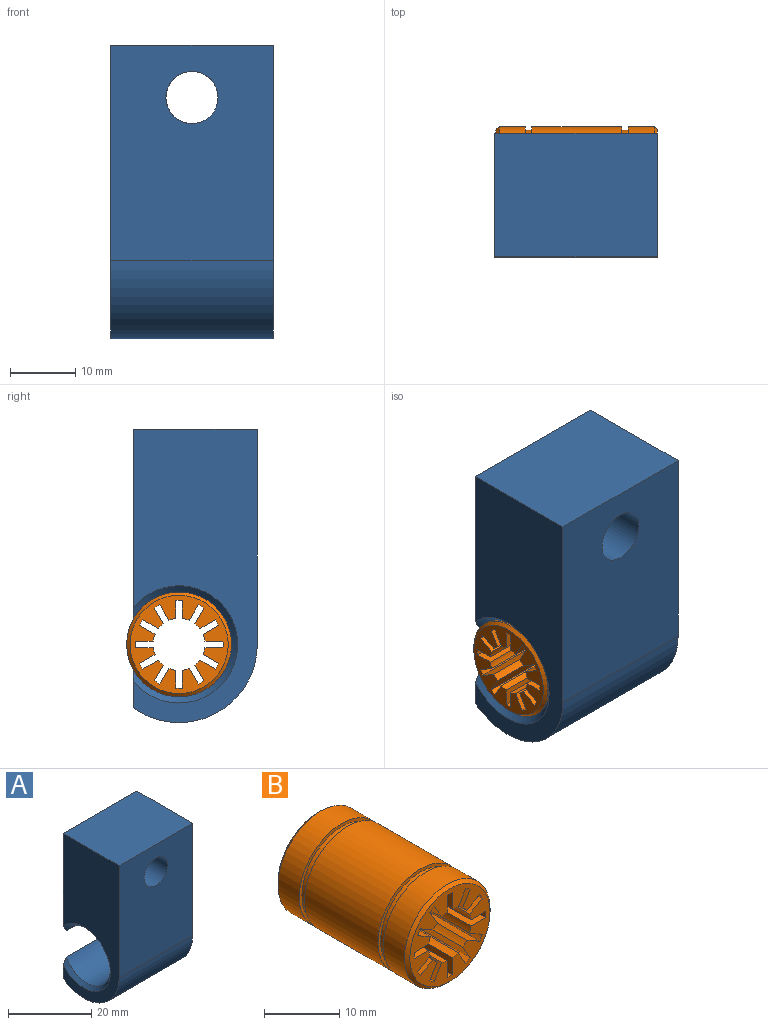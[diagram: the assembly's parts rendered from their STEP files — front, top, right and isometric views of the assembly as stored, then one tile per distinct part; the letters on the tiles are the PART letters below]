
ASSEMBLY  parts=2 mates=1
PART A: 11 faces, bbox 25x19.9x45 mm
  f0: plane 25x19mm, normal (0,0,1), area 475mm2, adj f3,f4,f7,f8
  f1: cylinder r=12mm len=25mm, axis (-1,0,0), area 658.1mm2, adj f3,f4,f7,f9
  f2: cylinder r=8mm len=23mm, axis (-1,0,0), area 970.1mm2, adj f5,f6,f8,f9
  f3: plane 45x19mm, normal (1,0,0), area 580mm2, adj f0,f1,f6,f7,f8,f9
  f4: plane 45x19mm, normal (-1,0,0), area 580mm2, adj f0,f1,f5,f7,f8,f9
  f5: cone r=9mm half-angle=45deg, axis (-1,0,0), area 61.1mm2, adj f2,f4,f8,f9
  f6: cone r=8mm half-angle=45deg, axis (1,0,0), area 61.1mm2, adj f2,f3,f8,f9
  f7: plane 33x25mm, normal (0,-1,0), area 774.7mm2, adj f0,f1,f3,f4,f10
  f8: plane 29.13x25mm, normal (0,1,0), area 676mm2, adj f0,f2,f3,f4,f5,f6,f10
  f9: plane 25x5.87mm, normal (0,1,0), area 145mm2, adj f1,f2,f3,f4,f5,f6
  f10: cylinder r=4mm len=19mm, axis (0,-1,0), area 477.5mm2, adj f7,f8
PART B: 61 faces, bbox 16.1x24.8x16.1 mm
  f0: plane 15.08x15.08mm, normal (0,1,0), area 95.2mm2, adj f12,f13,f14,f15,f16,f17,f18,f19
  f1: cylinder r=8.04mm len=16.08mm, axis (0,1,0), area 202mm2, adj f2,f12
  f2: plane 16.08x16.08mm, normal (0,-1,0), area 24.5mm2, adj f1,f3
  f3: cylinder r=7.54mm len=15.08mm, axis (0,1,0), area 47.4mm2, adj f2,f4
  f4: plane 16.08x16.08mm, normal (0,1,0), area 24.5mm2, adj f3,f5
  f5: cylinder r=8.04mm len=16.08mm, axis (0,1,0), area 697mm2, adj f4,f6
  f6: plane 16.08x16.08mm, normal (0,-1,0), area 24.5mm2, adj f5,f7
  f7: cylinder r=7.54mm len=15.08mm, axis (0,1,0), area 47.4mm2, adj f6,f8
  f8: plane 16.08x16.08mm, normal (0,1,0), area 24.5mm2, adj f7,f9
  f9: cylinder r=8.04mm len=16.08mm, axis (0,1,0), area 202mm2, adj f8,f11
  f10: plane 15.08x15.08mm, normal (0,-1,0), area 95.2mm2, adj f11,f13,f14,f15,f16,f17,f18,f19
  f11: cone r=8.04mm half-angle=45deg, axis (0,1,0), area 34.6mm2, adj f9,f10
  f12: cone r=7.54mm half-angle=45deg, axis (0,-1,0), area 34.6mm2, adj f0,f1
  f13: cylinder r=6.75mm len=24.8mm, axis (0,1,0), area 24.8mm2, adj f0,f10,f14,f60
  f14: plane 24.8x2.76mm, normal (-1,0,0), area 68.5mm2, adj f0,f10,f13,f15
  f15: cylinder r=4mm len=24.8mm, axis (0,1,0), area 27.1mm2, adj f0,f10,f14,f16
  f16: plane 24.8x2.39mm, normal (0.87,0,0.5), area 68.5mm2, adj f0,f10,f15,f17
  f17: cylinder r=6.75mm len=24.8mm, axis (0,1,0), area 24.8mm2, adj f0,f10,f16,f18
  f18: plane 24.8x2.39mm, normal (-0.87,0,-0.5), area 68.5mm2, adj f0,f10,f17,f19
  f19: cylinder r=4mm len=24.8mm, axis (0,1,0), area 27.1mm2, adj f0,f10,f18,f20
  f20: plane 24.8x2.39mm, normal (0.5,0,0.87), area 68.5mm2, adj f0,f10,f19,f21
  f21: cylinder r=6.75mm len=24.8mm, axis (0,1,0), area 24.8mm2, adj f0,f10,f20,f22
  f22: plane 24.8x2.39mm, normal (-0.5,0,-0.87), area 68.5mm2, adj f0,f10,f21,f23
  f23: cylinder r=4mm len=24.8mm, axis (0,1,0), area 27.1mm2, adj f0,f10,f22,f24
  f24: plane 24.8x2.76mm, normal (0,0,1), area 68.5mm2, adj f0,f10,f23,f25
  f25: cylinder r=6.75mm len=24.8mm, axis (0,1,0), area 24.8mm2, adj f0,f10,f24,f26
  f26: plane 24.8x2.76mm, normal (0,0,-1), area 68.5mm2, adj f0,f10,f25,f27
  f27: cylinder r=4mm len=24.8mm, axis (0,1,0), area 27.1mm2, adj f0,f10,f26,f28
  f28: plane 24.8x2.39mm, normal (-0.5,0,0.87), area 68.5mm2, adj f0,f10,f27,f29
  f29: cylinder r=6.75mm len=24.8mm, axis (0,1,0), area 24.8mm2, adj f0,f10,f28,f30
  f30: plane 24.8x2.39mm, normal (0.5,0,-0.87), area 68.5mm2, adj f0,f10,f29,f31
  f31: cylinder r=4mm len=24.8mm, axis (0,1,0), area 27.1mm2, adj f0,f10,f30,f32
  f32: plane 24.8x2.39mm, normal (-0.87,0,0.5), area 68.5mm2, adj f0,f10,f31,f33
  f33: cylinder r=6.75mm len=24.8mm, axis (0,1,0), area 24.8mm2, adj f0,f10,f32,f34
  f34: plane 24.8x2.39mm, normal (0.87,0,-0.5), area 68.5mm2, adj f0,f10,f33,f35
  f35: cylinder r=4mm len=24.8mm, axis (0,1,0), area 27.1mm2, adj f0,f10,f34,f36
  f36: plane 24.8x2.76mm, normal (-1,0,0), area 68.5mm2, adj f0,f10,f35,f37
  f37: cylinder r=6.75mm len=24.8mm, axis (0,1,0), area 24.8mm2, adj f0,f10,f36,f38
  f38: plane 24.8x2.76mm, normal (1,0,0), area 68.5mm2, adj f0,f10,f37,f39
  f39: cylinder r=4mm len=24.8mm, axis (0,1,0), area 27.1mm2, adj f0,f10,f38,f40
  f40: plane 24.8x2.39mm, normal (-0.87,0,-0.5), area 68.5mm2, adj f0,f10,f39,f41
  f41: cylinder r=6.75mm len=24.8mm, axis (0,1,0), area 24.8mm2, adj f0,f10,f40,f42
  f42: plane 24.8x2.39mm, normal (0.87,0,0.5), area 68.5mm2, adj f0,f10,f41,f43
  f43: cylinder r=4mm len=24.8mm, axis (0,1,0), area 27.1mm2, adj f0,f10,f42,f44
  f44: plane 24.8x2.39mm, normal (-0.5,0,-0.87), area 68.5mm2, adj f0,f10,f43,f45
  f45: cylinder r=6.75mm len=24.8mm, axis (0,1,0), area 24.8mm2, adj f0,f10,f44,f46
  f46: plane 24.8x2.39mm, normal (0.5,0,0.87), area 68.5mm2, adj f0,f10,f45,f47
  f47: cylinder r=4mm len=24.8mm, axis (0,1,0), area 27.1mm2, adj f0,f10,f46,f48
  f48: plane 24.8x2.76mm, normal (0,0,-1), area 68.5mm2, adj f0,f10,f47,f49
  f49: cylinder r=6.75mm len=24.8mm, axis (0,1,0), area 24.8mm2, adj f0,f10,f48,f50
  f50: plane 24.8x2.76mm, normal (0,0,1), area 68.5mm2, adj f0,f10,f49,f51
  f51: cylinder r=4mm len=24.8mm, axis (0,1,0), area 27.1mm2, adj f0,f10,f50,f52
  f52: plane 24.8x2.39mm, normal (0.5,0,-0.87), area 68.5mm2, adj f0,f10,f51,f53
  f53: cylinder r=6.75mm len=24.8mm, axis (0,1,0), area 24.8mm2, adj f0,f10,f52,f54
  f54: plane 24.8x2.39mm, normal (-0.5,0,0.87), area 68.5mm2, adj f0,f10,f53,f55
  f55: cylinder r=4mm len=24.8mm, axis (0,1,0), area 27.1mm2, adj f0,f10,f54,f56
  f56: plane 24.8x2.39mm, normal (0.87,0,-0.5), area 68.5mm2, adj f0,f10,f55,f57
  f57: cylinder r=6.75mm len=24.8mm, axis (0,1,0), area 24.8mm2, adj f0,f10,f56,f58
  f58: plane 24.8x2.39mm, normal (-0.87,0,0.5), area 68.5mm2, adj f0,f10,f57,f59
  f59: cylinder r=4mm len=24.8mm, axis (0,1,0), area 27.1mm2, adj f0,f10,f58,f60
  f60: plane 24.8x2.76mm, normal (1,0,0), area 68.5mm2, adj f0,f10,f13,f59
PLACE A t=(0.24,8.7,-10.65)mm
PLACE B rot(axis=(0,0,1),90deg) t=(12.84,8.7,-10.65)mm
MATE fastened B.f1 <-> A.f1  axis (1,0,0) through (25.24,8.7,-10.65)mm
